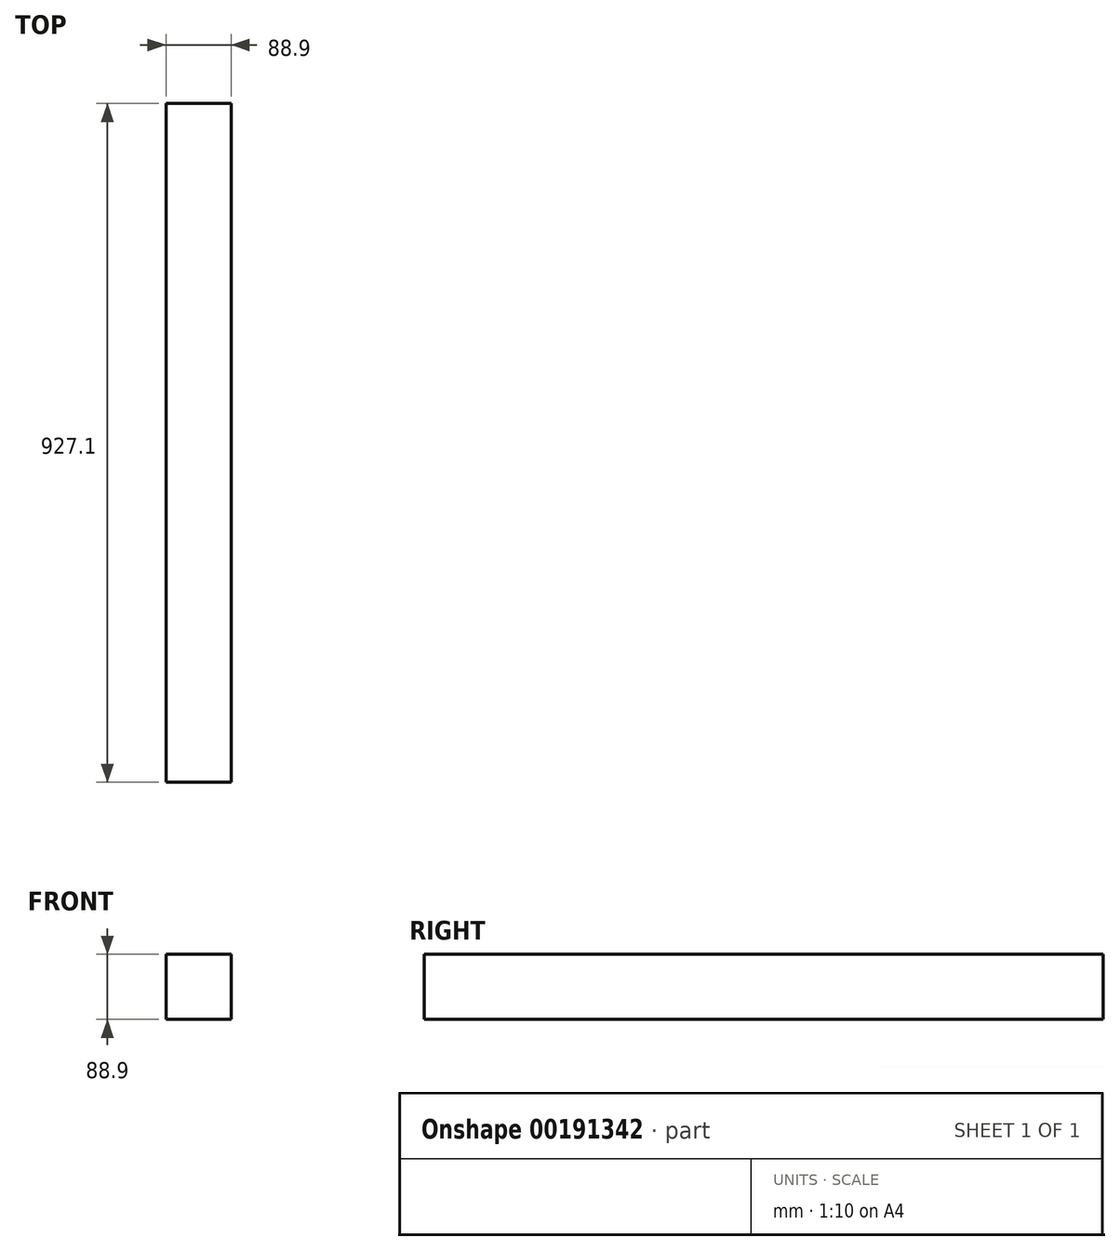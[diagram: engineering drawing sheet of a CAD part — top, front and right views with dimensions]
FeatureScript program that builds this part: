
annotation { "Feature Type Name" : "Feature", "Feature Type Description" : "" }
export const myFeature = defineFeature(function(context is Context, id is Id, definition is map)
    precondition{}
    {
        {
            var Q0;
            Q0=qCreatedBy(makeId("Front.planeOp"),FACE);
            var sketch = newSketch(context, id + "F0", { "sketchPlane" : qUnion([Q0])});
            skLineSegment(sketch, "E0.bottom", {"start": v(-44.45, 44.45) * mm, "end": v(44.45, 44.45) * mm});
            skLineSegment(sketch, "E0.top", {"start": v(-44.45, -44.45) * mm, "end": v(44.45, -44.45) * mm});
            skLineSegment(sketch, "E0.left", {"start": v(-44.45, 44.45) * mm, "end": v(-44.45, -44.45) * mm});
            skLineSegment(sketch, "E0.right", {"start": v(44.45, 44.45) * mm, "end": v(44.45, -44.45) * mm});
            skPoint(sketch, "E0.middle", {"position": v(0, 0) * mm});
            skPoint(sketch, "E1.visualSharp", {"position": v(-44.45, 44.45) * mm});
            skPoint(sketch, "E2.visualSharp", {"position": v(44.45, 44.45) * mm});
            skPoint(sketch, "E3.visualSharp", {"position": v(44.45, -44.45) * mm});
            skPoint(sketch, "E4.visualSharp", {"position": v(-44.45, -44.45) * mm});
            skSolve(sketch);
        }
        {
            var Q0;
            Q0=makeQuery(id+"F0.imprint","IMPRINT",FACE,{"disambiguationData":[TD([[makeQuery(id+"F0.imprint","IMPRINT",EDGE,{"derivedFrom":sQuery(id+"F0.wireOp",EDGE,"E0.bottom")}),-1.0]])]});
            extrude(context, id + "F1", {"entities" : qUnion([Q0]), "depth" : 927.1 * mm});
        }
    });
